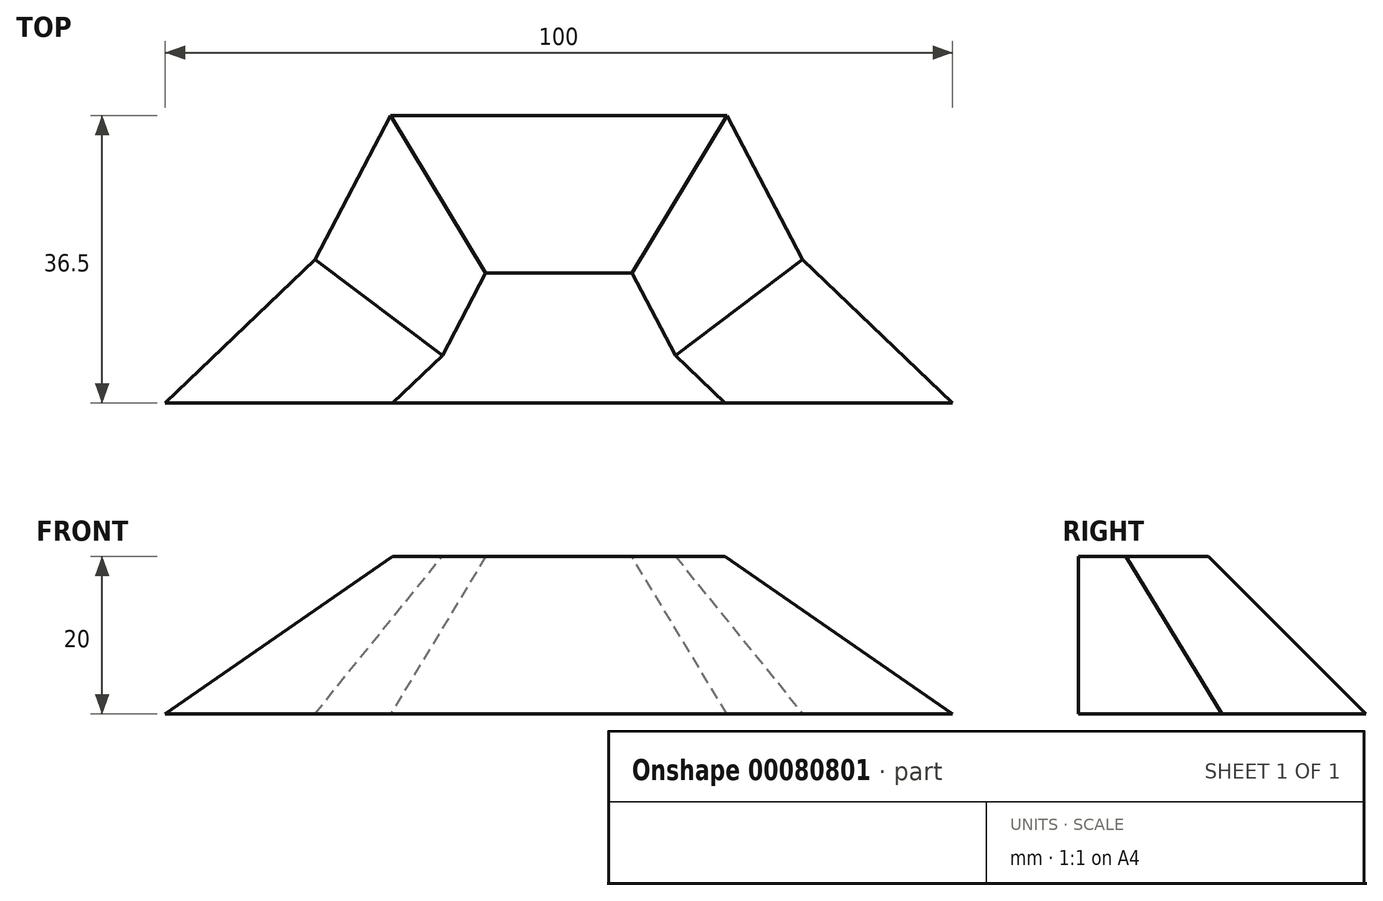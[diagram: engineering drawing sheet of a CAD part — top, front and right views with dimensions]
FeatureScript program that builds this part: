
annotation { "Feature Type Name" : "Feature", "Feature Type Description" : "" }
export const myFeature = defineFeature(function(context is Context, id is Id, definition is map)
    precondition{}
    {
        {
            var Q0;
            Q0=qCreatedBy(makeId("Top.planeOp"),FACE);
            var sketch = newSketch(context, id + "F0", { "sketchPlane" : qUnion([Q0])});
            skLineSegment(sketch, "E0.top", {"start": v(-50, -25) * mm, "end": v(50, -25) * mm});
            skPoint(sketch, "E0.middle", {"position": v(0, 0) * mm});
            skLineSegment(sketch, "E1", {"start": v(-21.35, 11.5) * mm, "end": v(21.35, 11.5) * mm});
            skLineSegment(sketch, "E2", {"start": v(-21.35, 11.5) * mm, "end": v(-30.98, -6.75) * mm});
            skLineSegment(sketch, "E3", {"start": v(-30.98, -6.75) * mm, "end": v(-50, -25) * mm});
            skLineSegment(sketch, "E4", {"start": v(21.35, 11.5) * mm, "end": v(30.98, -6.75) * mm});
            skLineSegment(sketch, "E5", {"start": v(30.98, -6.75) * mm, "end": v(50, -25) * mm});
            skSolve(sketch);
        }
        {
            var Q0;
            Q0=makeQuery(id+"F0.imprint","IMPRINT",FACE,{"disambiguationData":[TD([[makeQuery(id+"F0.imprint","IMPRINT",EDGE,{"derivedFrom":sQuery(id+"F0.wireOp",EDGE,"E0.top")}),1.0]])]});
            extrude(context, id + "F1", {"entities" : qUnion([Q0]), "depth" : 20 * mm});
        }
        {
            var Q0;
            Q0=makeQuery(id+"F1.opExtrude","CAP_EDGE",EDGE,{"disambiguationData":[OSD([sQuery(id+"F0.wireOp",EDGE,"E1")])],"isStart":false});
            var Q1;
            Q1=makeQuery(id+"F1.opExtrude","CAP_EDGE",EDGE,{"disambiguationData":[OSD([sQuery(id+"F0.wireOp",EDGE,"E4")])],"isStart":false});
            var Q2;
            Q2=makeQuery(id+"F1.opExtrude","CAP_EDGE",EDGE,{"disambiguationData":[OSD([sQuery(id+"F0.wireOp",EDGE,"E5")])],"isStart":false});
            var Q3;
            Q3=makeQuery(id+"F1.opExtrude","CAP_EDGE",EDGE,{"disambiguationData":[OSD([sQuery(id+"F0.wireOp",EDGE,"E3")])],"isStart":false});
            var Q4;
            Q4=makeQuery(id+"F1.opExtrude","CAP_EDGE",EDGE,{"disambiguationData":[OSD([sQuery(id+"F0.wireOp",EDGE,"E2")])],"isStart":false});
            chamfer(context, id + "F2", {"entities" : qUnion([Q0, Q1, Q2, Q3, Q4]), "width" : 20 * mm, "tangentPropagation" : true});
        }
    });
